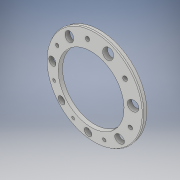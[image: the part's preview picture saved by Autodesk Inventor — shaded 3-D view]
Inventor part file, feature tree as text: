
AUTODESK INVENTOR PART (.ipt)
format: ipt  version: 2018 (Build 220112000, 112)  size: 160,256 bytes
history: native  units: mm
features: extrude x1, fillet x1, sketch x1
ambient origin geometry x8: Origin, YZ Plane, XZ Plane, XY Plane, X Axis, Y Axis, Z Axis, Center Point
bodies: Solid1 (feature_tree)
feature tree (3):
  extrude  "Extrusion1"  Depth=1.0mm
  fillet  "Fillet1"  Radius=110.0mm
  sketch  "Sketch1"  dims[d0=90.0mm d1=130.0mm d2=110.0mm d3=12.0mm d4=5.0mm d5=70.0mm d7=360.0deg d9=6.0mm d10=0.0mm d11=1.0mm]
